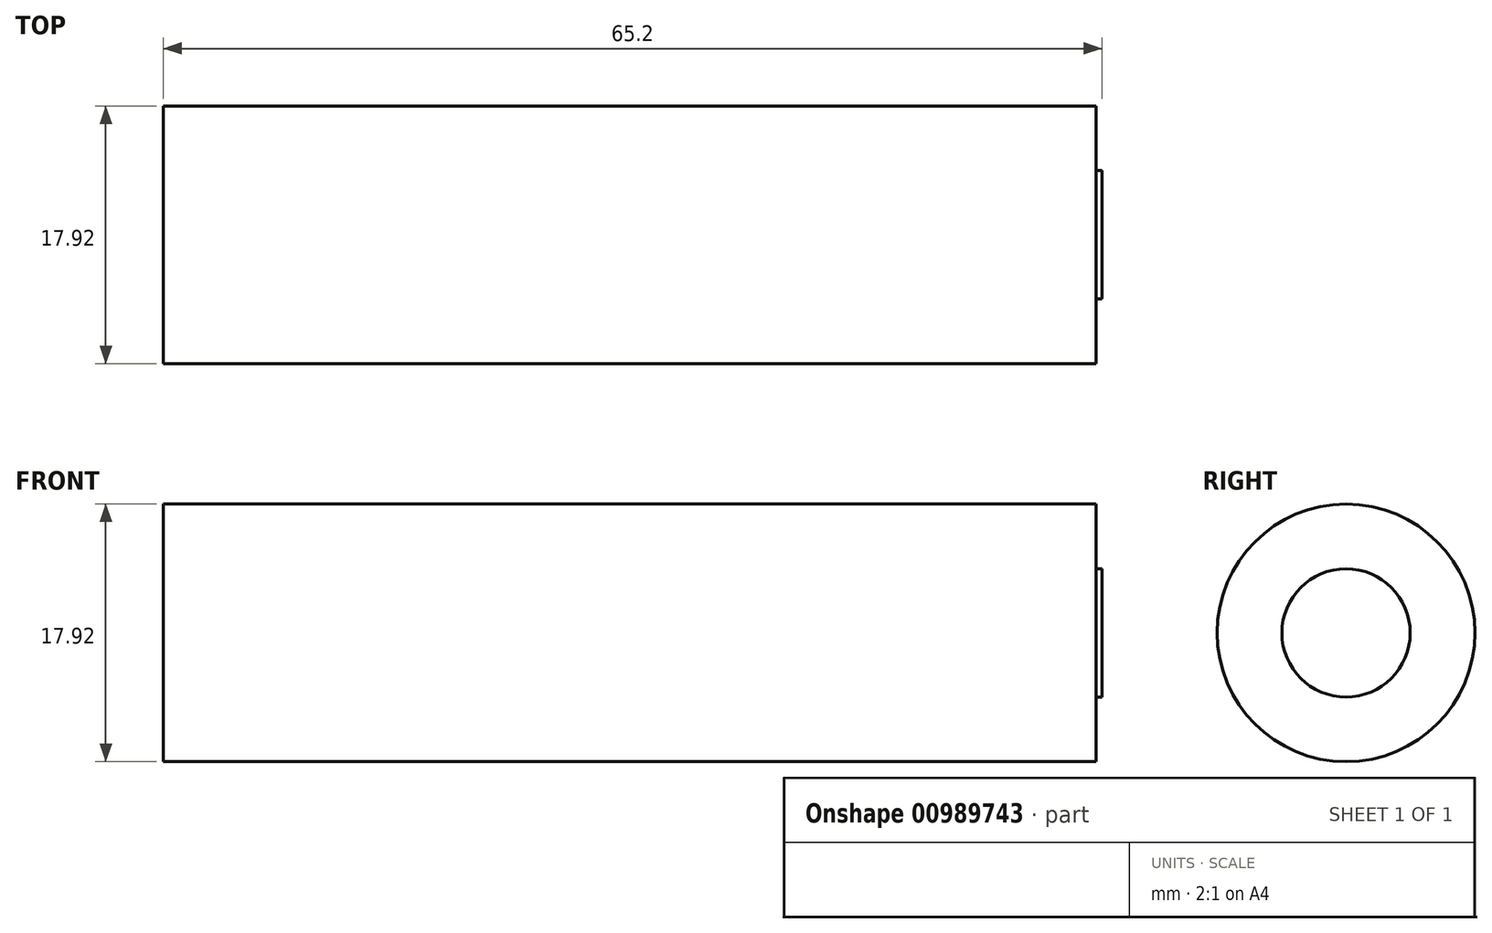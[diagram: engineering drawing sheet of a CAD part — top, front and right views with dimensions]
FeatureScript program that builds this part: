
annotation { "Feature Type Name" : "Feature", "Feature Type Description" : "" }
export const myFeature = defineFeature(function(context is Context, id is Id, definition is map)
    precondition{}
    {
        {
            var Q0;
            Q0=qCreatedBy(makeId("Top.planeOp"),FACE);
            var sketch = newSketch(context, id + "F0", { "sketchPlane" : qUnion([Q0])});
            skLineSegment(sketch, "E0", {"start": v(-41.79, 0) * mm, "end": v(-41.79, 8.96) * mm});
            skLineSegment(sketch, "E1", {"start": v(-41.79, 8.96) * mm, "end": v(23.01, 8.96) * mm});
            skLineSegment(sketch, "E2", {"start": v(23.01, 8.96) * mm, "end": v(23.01, 4.46) * mm});
            skLineSegment(sketch, "E3", {"start": v(23.01, 4.46) * mm, "end": v(23.41, 4.46) * mm});
            skLineSegment(sketch, "E4", {"start": v(23.41, 4.46) * mm, "end": v(23.41, 0) * mm});
            skLineSegment(sketch, "E5", {"start": v(-46.25, 0) * mm, "end": v(36.65, 0) * mm, "construction": true});
            skLineSegment(sketch, "E6", {"start": v(-41.79, 0) * mm, "end": v(23.41, 0) * mm});
            skSolve(sketch);
        }
        {
            var Q0;
            Q0 = qSketchRegion(id + "F0", true);
            var Q1;
            Q1=sQuery(id+"F0.wireOp",EDGE,"E5");
            revolve(context, id + "F1", {"surfaceOperationType" : NewSurfaceOperationType.NEW, "entities" : qUnion([Q0]), "axis" : qUnion([Q1]), "revolveType" : RevolveType.FULL});
        }
    });
